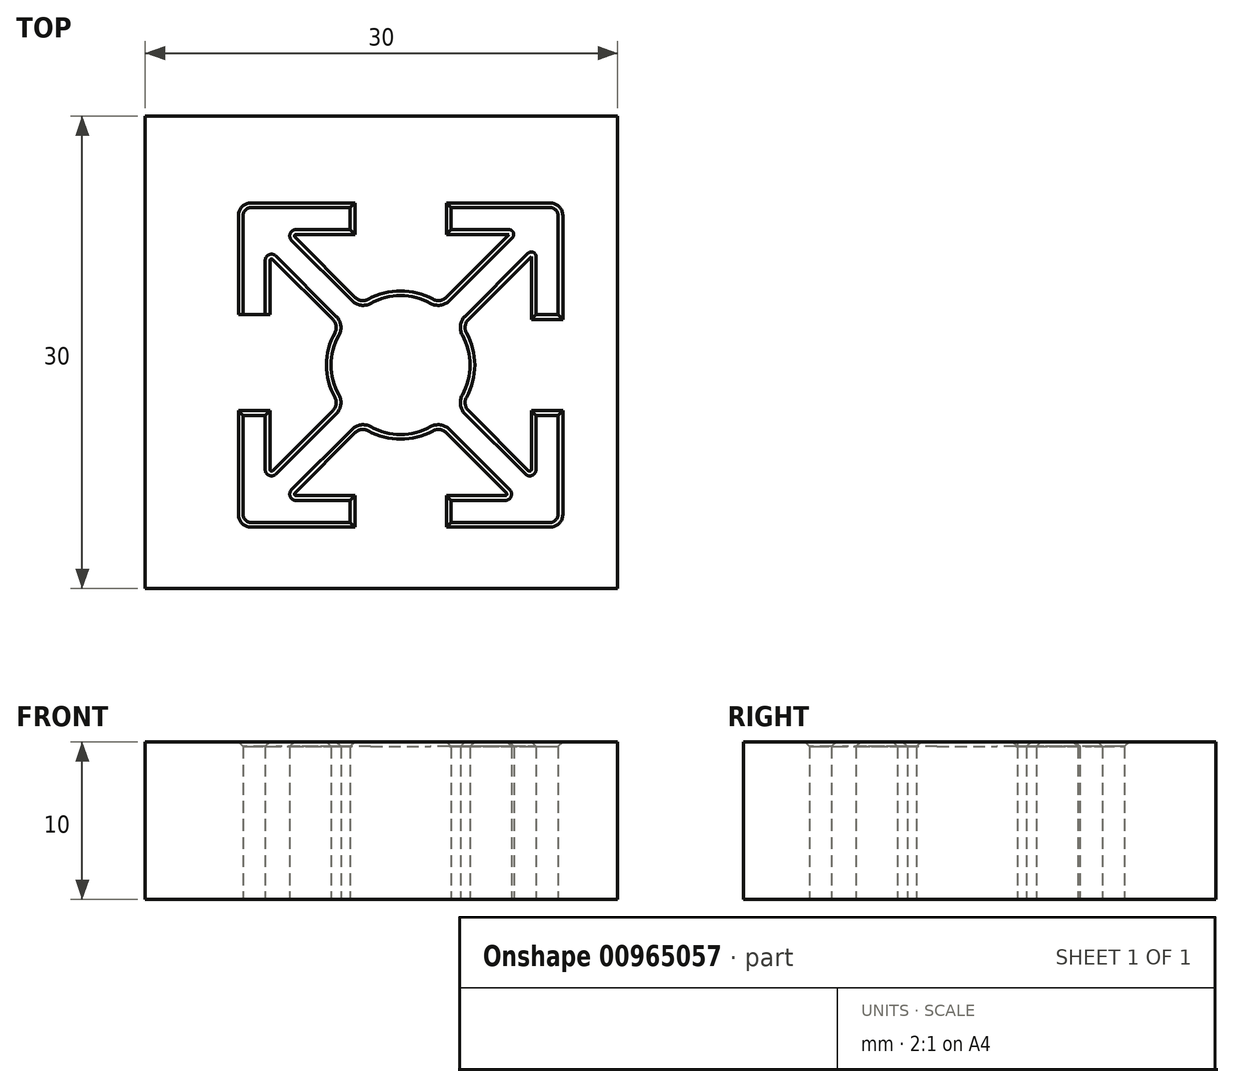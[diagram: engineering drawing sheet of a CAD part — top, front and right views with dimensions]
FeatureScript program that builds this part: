
annotation { "Feature Type Name" : "Feature", "Feature Type Description" : "" }
export const myFeature = defineFeature(function(context is Context, id is Id, definition is map)
    precondition{}
    {
        {
            var Q0;
            Q0=qCreatedBy(makeId("Top.planeOp"),FACE);
            var sketch = newSketch(context, id + "F0", { "sketchPlane" : qUnion([Q0])});
            skLineSegment(sketch, "E0.bottom", {"start": v(0, 0) * mm, "end": v(20, 0) * mm, "construction": true});
            skLineSegment(sketch, "E0.top", {"start": v(0, 20) * mm, "end": v(20, 20) * mm, "construction": true});
            skLineSegment(sketch, "E0.left", {"start": v(0, 0) * mm, "end": v(0, 20) * mm, "construction": true});
            skLineSegment(sketch, "E0.right", {"start": v(20, 0) * mm, "end": v(20, 20) * mm, "construction": true});
            skLineSegment(sketch, "E1", {"start": v(10, 20) * mm, "end": v(10, 0) * mm, "construction": true});
            skLineSegment(sketch, "E2", {"start": v(20, 10) * mm, "end": v(0, 10) * mm, "construction": true});
            skLineSegment(sketch, "E3", {"start": v(19.5, 20) * mm, "end": v(13.2, 20) * mm});
            skLineSegment(sketch, "E4", {"start": v(13.2, 20) * mm, "end": v(13.2, 18.6) * mm});
            skLineSegment(sketch, "E5", {"start": v(13.2, 18.6) * mm, "end": v(16.89, 18.6) * mm});
            skLineSegment(sketch, "E6", {"start": v(0, 0) * mm, "end": v(20, 20) * mm, "construction": true});
            skLineSegment(sketch, "E7", {"start": v(20, 0) * mm, "end": v(0, 20) * mm, "construction": true});
            skLineSegment(sketch, "E8", {"start": v(17.1, 18.09) * mm, "end": v(13.1, 14.08) * mm});
            skLineSegment(sketch, "E9", {"start": v(20, 13.2) * mm, "end": v(18.6, 13.2) * mm});
            skLineSegment(sketch, "E10", {"start": v(18.6, 13.2) * mm, "end": v(18.6, 16.89) * mm});
            skLineSegment(sketch, "E11", {"start": v(18.09, 17.1) * mm, "end": v(14.08, 13.1) * mm});
            skLineSegment(sketch, "E12", {"start": v(20, 0.5) * mm, "end": v(20, 6.8) * mm});
            skLineSegment(sketch, "E13", {"start": v(20, 6.8) * mm, "end": v(18.6, 6.8) * mm});
            skLineSegment(sketch, "E14", {"start": v(18.6, 6.8) * mm, "end": v(18.6, 3.36) * mm});
            skLineSegment(sketch, "E15", {"start": v(17.92, 3.07) * mm, "end": v(14.08, 6.9) * mm});
            skLineSegment(sketch, "E16", {"start": v(13.2, 0) * mm, "end": v(13.2, 1.4) * mm});
            skLineSegment(sketch, "E17", {"start": v(13.2, 1.4) * mm, "end": v(16.64, 1.4) * mm});
            skLineSegment(sketch, "E18", {"start": v(16.93, 2.08) * mm, "end": v(13.1, 5.92) * mm});
            skLineSegment(sketch, "E19", {"start": v(6.8, 0) * mm, "end": v(6.8, 1.4) * mm});
            skLineSegment(sketch, "E20", {"start": v(6.8, 1.4) * mm, "end": v(3.36, 1.4) * mm});
            skLineSegment(sketch, "E21", {"start": v(3.07, 2.08) * mm, "end": v(6.9, 5.92) * mm});
            skLineSegment(sketch, "E22", {"start": v(6.8, 0) * mm, "end": v(0.5, 0) * mm});
            skLineSegment(sketch, "E23", {"start": v(0, 6.8) * mm, "end": v(1.4, 6.8) * mm});
            skLineSegment(sketch, "E24", {"start": v(1.4, 6.8) * mm, "end": v(1.4, 3.36) * mm});
            skLineSegment(sketch, "E25", {"start": v(2.08, 3.07) * mm, "end": v(5.92, 6.9) * mm});
            skLineSegment(sketch, "E26", {"start": v(0, 19.5) * mm, "end": v(0, 13.2) * mm});
            skLineSegment(sketch, "E27", {"start": v(0, 13.2) * mm, "end": v(1.4, 13.2) * mm});
            skLineSegment(sketch, "E28", {"start": v(1.4, 13.2) * mm, "end": v(1.4, 16.64) * mm});
            skLineSegment(sketch, "E29", {"start": v(2.08, 16.93) * mm, "end": v(5.92, 13.1) * mm});
            skLineSegment(sketch, "E30", {"start": v(6.8, 20) * mm, "end": v(6.8, 18.6) * mm});
            skLineSegment(sketch, "E31", {"start": v(6.8, 18.6) * mm, "end": v(3.36, 18.6) * mm});
            skLineSegment(sketch, "E32", {"start": v(3.07, 17.92) * mm, "end": v(6.9, 14.08) * mm});
            skLineSegment(sketch, "E33", {"start": v(20, 13.2) * mm, "end": v(20, 19.5) * mm});
            skLineSegment(sketch, "E34", {"start": v(6.8, 20) * mm, "end": v(0.5, 20) * mm});
            skLineSegment(sketch, "E35", {"start": v(0, 6.8) * mm, "end": v(0, 0.5) * mm});
            skLineSegment(sketch, "E36", {"start": v(13.2, 0) * mm, "end": v(19.5, 0) * mm});
            skArc(sketch, "E37", {"start": v(11.9, 13.92) * mm, "mid": v(10, 14.41) * mm, "end": v(8.1, 13.92) * mm});
            skArc(sketch, "E38", {"start": v(13.92, 8.1) * mm, "mid": v(14.41, 10) * mm, "end": v(13.92, 11.9) * mm});
            skArc(sketch, "E39", {"start": v(8.1, 6.08) * mm, "mid": v(10, 5.59) * mm, "end": v(11.9, 6.08) * mm});
            skArc(sketch, "E40", {"start": v(6.08, 11.9) * mm, "mid": v(5.59, 10) * mm, "end": v(6.08, 8.1) * mm});
            skPoint(sketch, "E41", {"position": v(10, 10) * mm});
            skPoint(sketch, "E42.visualSharp", {"position": v(2.39, 18.6) * mm});
            skArc(sketch, "E42.filletArc", {"start": v(3.36, 18.6) * mm, "mid": v(2.99, 18.35) * mm, "end": v(3.07, 17.92) * mm});
            skPoint(sketch, "E43.visualSharp", {"position": v(17.61, 18.6) * mm});
            skArc(sketch, "E43.filletArc", {"start": v(17.1, 18.09) * mm, "mid": v(17.16, 18.41) * mm, "end": v(16.89, 18.6) * mm});
            skPoint(sketch, "E44.visualSharp", {"position": v(18.6, 17.61) * mm});
            skArc(sketch, "E44.filletArc", {"start": v(18.6, 16.89) * mm, "mid": v(18.41, 17.16) * mm, "end": v(18.09, 17.1) * mm});
            skPoint(sketch, "E45.visualSharp", {"position": v(18.6, 2.39) * mm});
            skArc(sketch, "E45.filletArc", {"start": v(17.92, 3.07) * mm, "mid": v(18.35, 2.99) * mm, "end": v(18.6, 3.36) * mm});
            skPoint(sketch, "E46.visualSharp", {"position": v(17.61, 1.4) * mm});
            skArc(sketch, "E46.filletArc", {"start": v(16.64, 1.4) * mm, "mid": v(17.01, 1.65) * mm, "end": v(16.93, 2.08) * mm});
            skPoint(sketch, "E47.visualSharp", {"position": v(2.39, 1.4) * mm});
            skArc(sketch, "E47.filletArc", {"start": v(3.07, 2.08) * mm, "mid": v(2.99, 1.65) * mm, "end": v(3.36, 1.4) * mm});
            skPoint(sketch, "E48.visualSharp", {"position": v(1.4, 2.39) * mm});
            skArc(sketch, "E48.filletArc", {"start": v(1.4, 3.36) * mm, "mid": v(1.65, 2.99) * mm, "end": v(2.08, 3.07) * mm});
            skPoint(sketch, "E49.visualSharp", {"position": v(1.4, 17.61) * mm});
            skArc(sketch, "E49.filletArc", {"start": v(2.08, 16.93) * mm, "mid": v(1.65, 17.01) * mm, "end": v(1.4, 16.64) * mm});
            skPoint(sketch, "E50.visualSharp", {"position": v(7.49, 13.5) * mm});
            skArc(sketch, "E50.filletArc", {"start": v(6.9, 14.08) * mm, "mid": v(7.47, 13.8) * mm, "end": v(8.1, 13.92) * mm});
            skPoint(sketch, "E51.visualSharp", {"position": v(12.51, 13.5) * mm});
            skArc(sketch, "E51.filletArc", {"start": v(11.9, 13.92) * mm, "mid": v(12.53, 13.8) * mm, "end": v(13.1, 14.08) * mm});
            skPoint(sketch, "E52.visualSharp", {"position": v(13.5, 12.51) * mm});
            skArc(sketch, "E52.filletArc", {"start": v(14.08, 13.1) * mm, "mid": v(13.8, 12.53) * mm, "end": v(13.92, 11.9) * mm});
            skPoint(sketch, "E53.visualSharp", {"position": v(13.5, 7.49) * mm});
            skArc(sketch, "E53.filletArc", {"start": v(13.92, 8.1) * mm, "mid": v(13.8, 7.47) * mm, "end": v(14.08, 6.9) * mm});
            skPoint(sketch, "E54.visualSharp", {"position": v(12.51, 6.5) * mm});
            skArc(sketch, "E54.filletArc", {"start": v(13.1, 5.92) * mm, "mid": v(12.53, 6.2) * mm, "end": v(11.9, 6.08) * mm});
            skPoint(sketch, "E55.visualSharp", {"position": v(7.49, 6.5) * mm});
            skArc(sketch, "E55.filletArc", {"start": v(8.1, 6.08) * mm, "mid": v(7.47, 6.2) * mm, "end": v(6.9, 5.92) * mm});
            skPoint(sketch, "E56.visualSharp", {"position": v(6.5, 7.49) * mm});
            skArc(sketch, "E56.filletArc", {"start": v(5.92, 6.9) * mm, "mid": v(6.2, 7.47) * mm, "end": v(6.08, 8.1) * mm});
            skPoint(sketch, "E57.visualSharp", {"position": v(6.5, 12.51) * mm});
            skArc(sketch, "E57.filletArc", {"start": v(6.08, 11.9) * mm, "mid": v(6.2, 12.53) * mm, "end": v(5.92, 13.1) * mm});
            skPoint(sketch, "E58.visualSharp", {"position": v(0, 20) * mm});
            skArc(sketch, "E58.filletArc", {"start": v(0.5, 20) * mm, "mid": v(0.15, 19.85) * mm, "end": v(0, 19.5) * mm});
            skPoint(sketch, "E59.visualSharp", {"position": v(20, 20) * mm});
            skArc(sketch, "E59.filletArc", {"start": v(20, 19.5) * mm, "mid": v(19.85, 19.85) * mm, "end": v(19.5, 20) * mm});
            skPoint(sketch, "E60.visualSharp", {"position": v(20, 0) * mm});
            skArc(sketch, "E60.filletArc", {"start": v(19.5, 0) * mm, "mid": v(19.85, 0.15) * mm, "end": v(20, 0.5) * mm});
            skPoint(sketch, "E61.visualSharp", {"position": v(0, 0) * mm});
            skArc(sketch, "E61.filletArc", {"start": v(0, 0.5) * mm, "mid": v(0.15, 0.15) * mm, "end": v(0.5, 0) * mm});
            skLineSegment(sketch, "E62.bottom", {"start": v(-6.22, 25.81) * mm, "end": v(23.78, 25.81) * mm});
            skLineSegment(sketch, "E62.top", {"start": v(-6.22, -4.19) * mm, "end": v(23.78, -4.19) * mm});
            skLineSegment(sketch, "E62.left", {"start": v(-6.22, 25.81) * mm, "end": v(-6.22, -4.19) * mm});
            skLineSegment(sketch, "E62.right", {"start": v(23.78, 25.81) * mm, "end": v(23.78, -4.19) * mm});
            skSolve(sketch);
        }
        {
            var Q0;
            Q0=makeQuery(id+"F0.imprint","IMPRINT",FACE,{"disambiguationData":[TD([[makeQuery(id+"F0.imprint","IMPRINT",EDGE,{"derivedFrom":sQuery(id+"F0.wireOp",EDGE,"E3")}),-1.0]])]});
            extrude(context, id + "F1", {"entities" : qUnion([Q0]), "depth" : 10 * mm, "offsetDistance" : 25 * mm});
        }
        {
            var Q0;
            Q0=makeQuery(id+"F1.opExtrude","CAP_EDGE",EDGE,{"disambiguationData":[OSD([sQuery(id+"F0.wireOp",EDGE,"E26")])],"isStart":false});
            var Q1;
            Q1=makeQuery(id+"F1.opExtrude","CAP_EDGE",EDGE,{"disambiguationData":[OSD([sQuery(id+"F0.wireOp",EDGE,"E32")])],"isStart":false});
            var Q2;
            Q2=makeQuery(id+"F1.opExtrude","CAP_EDGE",EDGE,{"disambiguationData":[OSD([sQuery(id+"F0.wireOp",EDGE,"E29")])],"isStart":false});
            var Q3;
            Q3=makeQuery(id+"F1.opExtrude","CAP_EDGE",EDGE,{"disambiguationData":[OSD([sQuery(id+"F0.wireOp",EDGE,"E55.filletArc")])],"isStart":false});
            var Q4;
            Q4=makeQuery(id+"F1.opExtrude","CAP_EDGE",EDGE,{"disambiguationData":[OSD([sQuery(id+"F0.wireOp",EDGE,"E38")])],"isStart":false});
            var Q5;
            Q5=makeQuery(id+"F1.opExtrude","CAP_EDGE",EDGE,{"disambiguationData":[OSD([sQuery(id+"F0.wireOp",EDGE,"E9")])],"isStart":false});
            var Q6;
            Q6=makeQuery(id+"F1.opExtrude","CAP_EDGE",EDGE,{"disambiguationData":[OSD([sQuery(id+"F0.wireOp",EDGE,"E3")])],"isStart":false});
            var Q7;
            Q7=makeQuery(id+"F1.opExtrude","CAP_EDGE",EDGE,{"disambiguationData":[OSD([sQuery(id+"F0.wireOp",EDGE,"E4")])],"isStart":false});
            var Q8;
            Q8=makeQuery(id+"F1.opExtrude","CAP_EDGE",EDGE,{"disambiguationData":[OSD([sQuery(id+"F0.wireOp",EDGE,"E30")])],"isStart":false});
            var Q9;
            Q9=makeQuery(id+"F1.opExtrude","CAP_EDGE",EDGE,{"disambiguationData":[OSD([sQuery(id+"F0.wireOp",EDGE,"E12")])],"isStart":false});
            var Q10;
            Q10=makeQuery(id+"F1.opExtrude","CAP_EDGE",EDGE,{"disambiguationData":[OSD([sQuery(id+"F0.wireOp",EDGE,"E16")])],"isStart":false});
            var Q11;
            Q11=makeQuery(id+"F1.opExtrude","CAP_EDGE",EDGE,{"disambiguationData":[OSD([sQuery(id+"F0.wireOp",EDGE,"E19")])],"isStart":false});
            var Q12;
            Q12=makeQuery(id+"F1.opExtrude","CAP_EDGE",EDGE,{"disambiguationData":[OSD([sQuery(id+"F0.wireOp",EDGE,"E23")])],"isStart":false});
            var Q13;
            Q13=makeQuery(id+"F1.opExtrude","CAP_EDGE",EDGE,{"disambiguationData":[OSD([sQuery(id+"F0.wireOp",EDGE,"E13")])],"isStart":false});
            var Q14;
            Q14=makeQuery(id+"F1.opExtrude","CAP_EDGE",EDGE,{"disambiguationData":[OSD([sQuery(id+"F0.wireOp",EDGE,"E35")])],"isStart":false});
            chamfer(context, id + "F2", {"entities" : qUnion([Q0, Q1, Q2, Q3, Q4, Q5, Q6, Q7, Q8, Q9, Q10, Q11, Q12, Q13, Q14]), "width" : 0.3 * mm, "tangentPropagation" : true});
        }
    });
